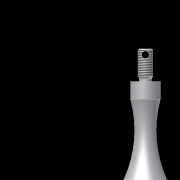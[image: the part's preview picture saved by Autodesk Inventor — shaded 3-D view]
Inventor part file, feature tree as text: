
AUTODESK INVENTOR PART (.ipt)
format: ipt  version: 2013 (Build 170138000, 138)  size: 160,256 bytes
history: native  units: mm
features: sketch x2, other x1, chamfer x1, thread x1, plane x1, hole x1, projected_geometry x1
ambient origin geometry x8: Origin, YZ Plane, XZ Plane, XY Plane, X Axis, Y Axis, Z Axis, Center Point
bodies: Volumenkörper1 (feature_tree)
feature tree (8):
  other  "Drehung1"
  chamfer  "Fase1"  Distance=3.0mm
  thread  "Gewinde1"  [1 undecoded]
  plane  "Arbeitsebene1"
  hole  "Bohrung1"  [1 undecoded]
  sketch  "Skizze1"  dims[d0=60.0mm]
  sketch  "Skizze2"  dims[d1=7.0mm d2=3.0mm d3=2.5mm d4=11.0mm d5=13.0mm d6=6.0mm d7=90.0deg d8=0.5mm d9=2.0mm d10=45.0deg d11=10.0mm d12=0.0mm d14=3.0mm d15=2.4mm d16=3.0mm d17=6.0mm d18=4.0mm d19=2.0mm d20=90.0deg d21=8.0mm d22=20.594885mm]
  projected_geometry  "Projizierte Kontur1"
note: 2 required parameter values undecoded (feature->parameter linkage not recoverable at this tier; creation-order binding heuristic only, values carry confidence <= 0.55)
